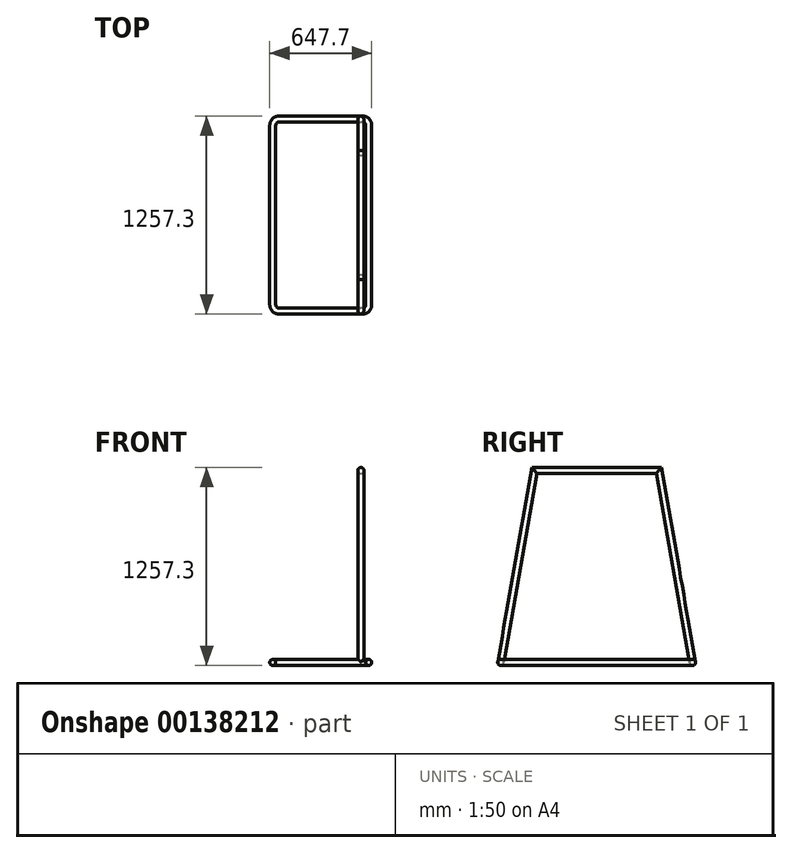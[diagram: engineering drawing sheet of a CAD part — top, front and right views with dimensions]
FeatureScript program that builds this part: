
annotation { "Feature Type Name" : "Feature", "Feature Type Description" : "" }
export const myFeature = defineFeature(function(context is Context, id is Id, definition is map)
    precondition{}
    {
        {
            var Q0;
            Q0=qCreatedBy(makeId("Top.planeOp"),FACE);
            var sketch = newSketch(context, id + "F0", { "sketchPlane" : qUnion([Q0])});
            skLineSegment(sketch, "E0.bottom", {"start": v(-267.46, 641.7) * mm, "end": v(265.94, 641.7) * mm});
            skLineSegment(sketch, "E0.top", {"start": v(-267.46, -577.5) * mm, "end": v(265.94, -577.5) * mm});
            skLineSegment(sketch, "E0.left", {"start": v(-305.56, 603.6) * mm, "end": v(-305.56, -539.4) * mm});
            skLineSegment(sketch, "E0.right", {"start": v(304.04, 603.6) * mm, "end": v(304.04, -539.4) * mm});
            skLineSegment(sketch, "E1", {"start": v(-0.76, 641.7) * mm, "end": v(-0.76, -577.5) * mm, "construction": true});
            skLineSegment(sketch, "E2", {"start": v(304.04, 32.1) * mm, "end": v(-305.56, 32.1) * mm, "construction": true});
            skPoint(sketch, "E3.visualSharp", {"position": v(-305.56, 641.7) * mm});
            skArc(sketch, "E3.filletArc", {"start": v(-267.46, 641.7) * mm, "mid": v(-294.4, 630.54) * mm, "end": v(-305.56, 603.6) * mm});
            skPoint(sketch, "E4.visualSharp", {"position": v(-305.56, -577.5) * mm});
            skArc(sketch, "E4.filletArc", {"start": v(-305.56, -539.4) * mm, "mid": v(-294.4, -566.35) * mm, "end": v(-267.46, -577.5) * mm});
            skPoint(sketch, "E5.visualSharp", {"position": v(304.04, -577.5) * mm});
            skArc(sketch, "E5.filletArc", {"start": v(265.94, -577.5) * mm, "mid": v(292.88, -566.35) * mm, "end": v(304.04, -539.4) * mm});
            skPoint(sketch, "E6.visualSharp", {"position": v(304.04, 641.7) * mm});
            skArc(sketch, "E6.filletArc", {"start": v(304.04, 603.6) * mm, "mid": v(292.88, 630.54) * mm, "end": v(265.94, 641.7) * mm});
            skSolve(sketch);
        }
        {
            var Q0;
            Q0=qCreatedBy(makeId("Right.planeOp"),FACE);
            var sketch = newSketch(context, id + "F1", { "sketchPlane" : qUnion([Q0])});
            skCircle(sketch, "E7", {"center": v(641.7, 0) * mm, "radius": 19.05 * mm});
            skSolve(sketch);
        }
        {
            var Q0;
            Q0 = qSketchRegion(id + "F1", true);
            var Q1;
            Q1 = qConstructionFilter(qBodyType(qCreatedBy(id + "F0" ,EDGE), BodyType.WIRE), ConstructionObject.NO);
            sweep(context, id + "F2", {"profiles" : qUnion([Q0]), "path" : qUnion([Q1])});
        }
        {
            var Q0;
            Q0=qCreatedBy(makeId("Right.planeOp"),FACE);
            cPlane(context, id + "F3", {"entities" : qUnion([Q0]), "cplaneType" : CPlaneType.OFFSET, "offset" : 254 * mm, "width" : 152.4 * mm, "height" : 152.4 * mm});
        }
        {
            var Q0;
            Q0=qCreatedBy(id+"F3.planeOp",FACE);
            var sketch = newSketch(context, id + "F4", { "sketchPlane" : qUnion([Q0])});
            skLineSegment(sketch, "E8", {"start": v(641.7, 0) * mm, "end": v(426.72, 1219.2) * mm});
            skLineSegment(sketch, "E9", {"start": v(426.72, 1219.2) * mm, "end": v(-362.53, 1219.2) * mm});
            skLineSegment(sketch, "E10", {"start": v(-362.53, 1219.2) * mm, "end": v(-577.5, 0) * mm});
            skSolve(sketch);
        }
        {
            var Q0;
            Q0=qCreatedBy(makeId("Front.planeOp"),FACE);
            var sketch = newSketch(context, id + "F5", { "sketchPlane" : qUnion([Q0])});
            skCircle(sketch, "E11", {"center": v(254, 1219.2) * mm, "radius": 19.05 * mm});
            skSolve(sketch);
        }
        {
            var Q0;
            Q0=makeQuery(id+"F5.imprint","IMPRINT",FACE,{"disambiguationData":[TD([[makeQuery(id+"F5.imprint","IMPRINT",EDGE,{"derivedFrom":sQuery(id+"F5.wireOp",EDGE,"E11")}),1.0]])]});
            var Q1;
            Q1=sQuery(id+"F4.wireOp",EDGE,"E8");
            var Q2;
            Q2=sQuery(id+"F4.wireOp",EDGE,"E9");
            var Q3;
            Q3=sQuery(id+"F4.wireOp",EDGE,"E10");
            sweep(context, id + "F6", {"operationType" : NewBodyOperationType.ADD, "profiles" : qUnion([Q0]), "path" : qUnion([Q1, Q2, Q3])});
        }
    });
